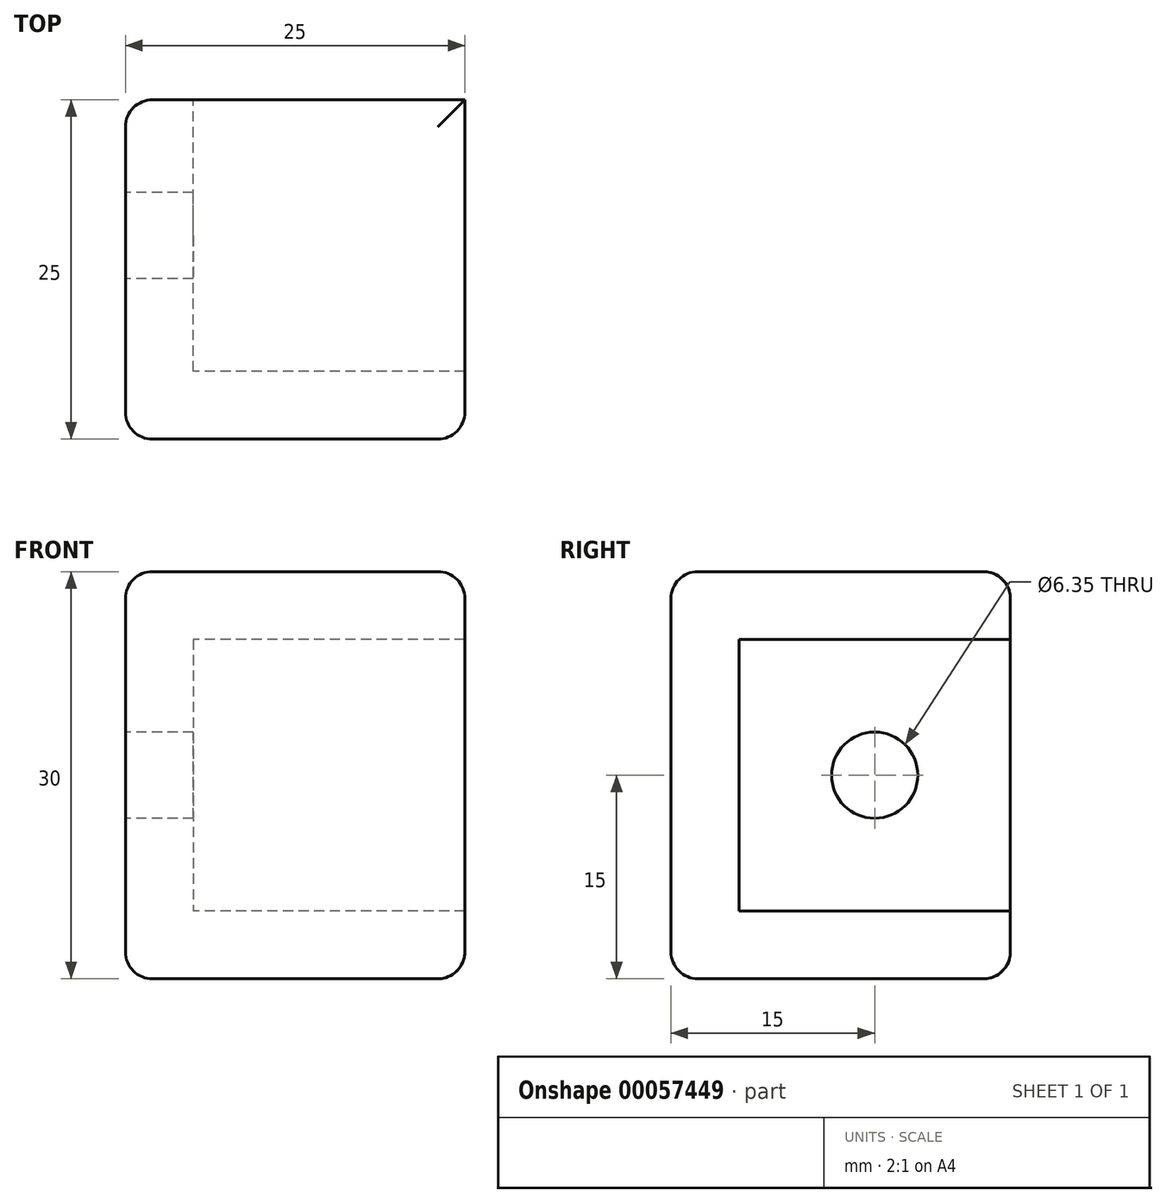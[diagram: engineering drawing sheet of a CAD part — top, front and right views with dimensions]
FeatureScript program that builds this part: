
annotation { "Feature Type Name" : "Feature", "Feature Type Description" : "" }
export const myFeature = defineFeature(function(context is Context, id is Id, definition is map)
    precondition{}
    {
        {
            var Q0;
            Q0=qCreatedBy(makeId("Front.planeOp"),FACE);
            var sketch = newSketch(context, id + "F0", { "sketchPlane" : qUnion([Q0])});
            skLineSegment(sketch, "E0.bottom", {"start": v(0, 0) * mm, "end": v(25, 0) * mm});
            skLineSegment(sketch, "E0.top", {"start": v(0, 30) * mm, "end": v(25, 30) * mm});
            skLineSegment(sketch, "E0.left", {"start": v(0, 0) * mm, "end": v(0, 30) * mm});
            skLineSegment(sketch, "E0.right", {"start": v(25, 0) * mm, "end": v(25, 30) * mm});
            skSolve(sketch);
        }
        {
            var Q0;
            Q0 = qSketchRegion(id + "F0", true);
            extrude(context, id + "F1", {"entities" : qUnion([Q0]), "endBound" : BoundingType.SYMMETRIC, "depth" : 25 * mm});
        }
        {
            var Q0;
            Q0=makeQuery(id+"F1.opExtrude","CAP_FACE",FACE,{"disambiguationData":[OSD([sQuery(id+"F0.wireOp",EDGE,"E0.bottom"),sQuery(id+"F0.wireOp",EDGE,"E0.top"),sQuery(id+"F0.wireOp",EDGE,"E0.left"),sQuery(id+"F0.wireOp",EDGE,"E0.right")])],"isStart":true});
            var sketch = newSketch(context, id + "F2", { "sketchPlane" : qUnion([Q0])});
            skLineSegment(sketch, "E1.bottom", {"start": v(-25, 25) * mm, "end": v(-5, 25) * mm});
            skLineSegment(sketch, "E1.top", {"start": v(-25, 5) * mm, "end": v(-5, 5) * mm});
            skLineSegment(sketch, "E1.left", {"start": v(-25, 25) * mm, "end": v(-25, 5) * mm});
            skLineSegment(sketch, "E1.right", {"start": v(-5, 25) * mm, "end": v(-5, 5) * mm});
            skSolve(sketch);
        }
        {
            var Q0;
            Q0 = qSketchRegion(id + "F2", true);
            extrude(context, id + "F3", {"entities" : qUnion([Q0]), "operationType" : NewBodyOperationType.REMOVE, "oppositeDirection" : true, "depth" : 20 * mm});
        }
        {
            var Q0;
            Q0=makeQuery(id+"F1.opExtrude","SWEPT_FACE",FACE,{"disambiguationData":[OSD([sQuery(id+"F0.wireOp",EDGE,"E0.left")])]});
            var sketch = newSketch(context, id + "F4", { "sketchPlane" : qUnion([Q0])});
            skCircle(sketch, "E2", {"center": v(-2.5, 15) * mm, "radius": 3.18 * mm});
            skSolve(sketch);
        }
        {
            var Q0;
            Q0 = qSketchRegion(id + "F4", true);
            extrude(context, id + "F5", {"entities" : qUnion([Q0]), "operationType" : NewBodyOperationType.REMOVE, "endBound" : BoundingType.THROUGH_ALL, "oppositeDirection" : true, "depth" : 25.4 * mm});
        }
        {
            var Q0;
            Q0=makeQuery(id+"F1.opExtrude","SWEPT_EDGE",EDGE,{"disambiguationData":[OSD([sQuery(id+"F0.wireOp",EDGE,"E0.top"),sQuery(id+"F0.wireOp",EDGE,"E0.left")])]});
            var Q1;
            Q1=makeQuery(id+"F1.opExtrude","CAP_EDGE",EDGE,{"disambiguationData":[OSD([sQuery(id+"F0.wireOp",EDGE,"E0.top")])],"isStart":true});
            var Q2;
            Q2=makeQuery(id+"F1.opExtrude","SWEPT_FACE",FACE,{"disambiguationData":[OSD([sQuery(id+"F0.wireOp",EDGE,"E0.top")])]});
            var Q3;
            Q3=makeQuery(id+"F1.opExtrude","CAP_FACE",FACE,{"disambiguationData":[OSD([sQuery(id+"F0.wireOp",EDGE,"E0.bottom"),sQuery(id+"F0.wireOp",EDGE,"E0.top"),sQuery(id+"F0.wireOp",EDGE,"E0.left"),sQuery(id+"F0.wireOp",EDGE,"E0.right")])],"isStart":false});
            var Q4;
            Q4=makeQuery(id+"F1.opExtrude","SWEPT_FACE",FACE,{"disambiguationData":[OSD([sQuery(id+"F0.wireOp",EDGE,"E0.bottom")])]});
            var Q5;
            Q5=makeQuery(id+"F1.opExtrude","CAP_EDGE",EDGE,{"disambiguationData":[OSD([sQuery(id+"F0.wireOp",EDGE,"E0.left")])],"isStart":true});
            fillet(context, id + "F6", {"entities" : qUnion([Q0, Q1, Q2, Q3, Q4, Q5]), "radius" : 2 * mm, "tangentPropagation" : true, "allowEdgeOverflow" : false});
        }
    });
